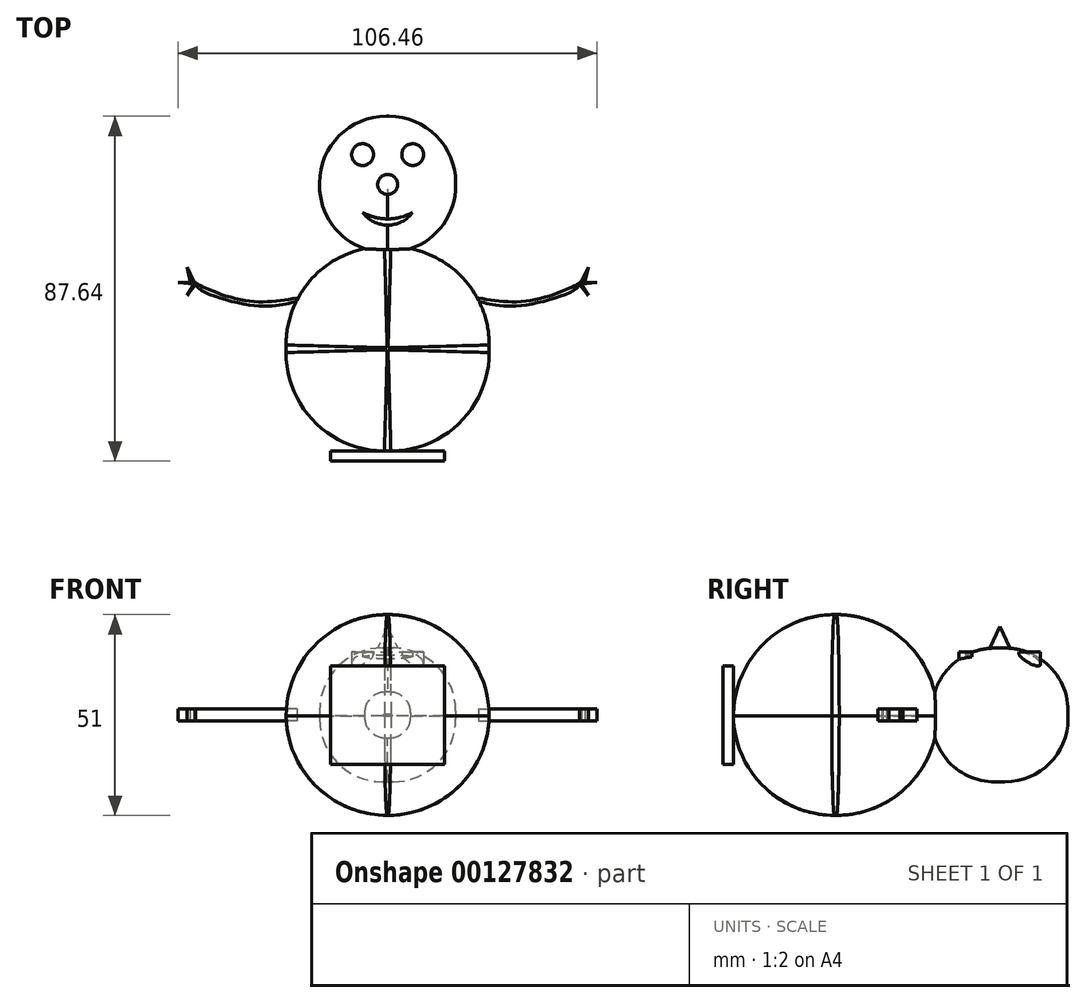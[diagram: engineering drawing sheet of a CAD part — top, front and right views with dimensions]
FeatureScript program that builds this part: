
annotation { "Feature Type Name" : "Feature", "Feature Type Description" : "" }
export const myFeature = defineFeature(function(context is Context, id is Id, definition is map)
    precondition{}
    {
        {
            var Q0;
            Q0=qCreatedBy(makeId("Top.planeOp"),FACE);
            var sketch = newSketch(context, id + "F0", { "sketchPlane" : qUnion([Q0])});
            skLineSegment(sketch, "E0.bottom", {"start": v(0.81, -25.96) * mm, "end": v(-0.81, -25.96) * mm});
            skLineSegment(sketch, "E0.top", {"start": v(0.81, 25.96) * mm, "end": v(-0.81, 25.96) * mm});
            skLineSegment(sketch, "E0.left", {"start": v(25.81, -0.96) * mm, "end": v(25.81, 0.96) * mm});
            skLineSegment(sketch, "E0.right", {"start": v(-25.81, -0.96) * mm, "end": v(-25.81, 0.96) * mm});
            skPoint(sketch, "E0.middle", {"position": v(0, 0) * mm});
            skPoint(sketch, "E1.visualSharp", {"position": v(-25.81, 25.96) * mm});
            skArc(sketch, "E1.filletArc", {"start": v(-0.81, 25.96) * mm, "mid": v(-18.49, 18.63) * mm, "end": v(-25.81, 0.96) * mm});
            skPoint(sketch, "E2.visualSharp", {"position": v(25.81, 25.96) * mm});
            skArc(sketch, "E2.filletArc", {"start": v(25.81, 0.96) * mm, "mid": v(18.49, 18.63) * mm, "end": v(0.81, 25.96) * mm});
            skPoint(sketch, "E3.visualSharp", {"position": v(25.81, -25.96) * mm});
            skArc(sketch, "E3.filletArc", {"start": v(0.81, -25.96) * mm, "mid": v(18.49, -18.63) * mm, "end": v(25.81, -0.96) * mm});
            skPoint(sketch, "E4.visualSharp", {"position": v(-25.81, -25.96) * mm});
            skArc(sketch, "E4.filletArc", {"start": v(-25.81, -0.96) * mm, "mid": v(-18.49, -18.63) * mm, "end": v(-0.81, -25.96) * mm});
            skSolve(sketch);
        }
        {
            var Q0;
            Q0 = qSketchRegion(id + "F0", true);
            extrude(context, id + "F1", {"entities" : qUnion([Q0]), "endBound" : BoundingType.SYMMETRIC, "depth" : 51 * mm});
        }
        {
            var Q0;
            Q0=makeQuery(id+"F1.opExtrude","SWEPT_EDGE",EDGE,{"disambiguationData":[OSD([sQuery(id+"F0.wireOp",EDGE,"E0.bottom"),sQuery(id+"F0.wireOp",EDGE,"E3.filletArc")])]});
            var Q1;
            Q1=makeQuery(id+"F1.opExtrude","CAP_EDGE",EDGE,{"disambiguationData":[OSD([sQuery(id+"F0.wireOp",EDGE,"E3.filletArc")])],"isStart":false});
            fillet(context, id + "F2", {"entities" : qUnion([Q0, Q1]), "radius" : 25.7 * mm, "tangentPropagation" : true, "allowEdgeOverflow" : false});
        }
        {
            var Q0;
            Q0=makeQuery(id+"F1.opExtrude","CAP_EDGE",EDGE,{"disambiguationData":[OSD([sQuery(id+"F0.wireOp",EDGE,"E3.filletArc")])],"isStart":true});
            var Q1;
            Q1=makeQuery(id+"F1.opExtrude","SWEPT_EDGE",EDGE,{"disambiguationData":[OSD([sQuery(id+"F0.wireOp",EDGE,"E0.bottom"),sQuery(id+"F0.wireOp",EDGE,"E3.filletArc")])]});
            fillet(context, id + "F3", {"entities" : qUnion([Q0, Q1]), "radius" : 25.7 * mm, "tangentPropagation" : true, "allowEdgeOverflow" : false});
        }
        {
            var Q0;
            Q0=qCreatedBy(makeId("Top.planeOp"),FACE);
            var sketch = newSketch(context, id + "F4", { "sketchPlane" : qUnion([Q0])});
            skPoint(sketch, "E5", {"position": v(0, 41.8) * mm});
            skLineSegment(sketch, "E6.bottom", {"start": v(0.3, 24.5) * mm, "end": v(-0.3, 24.5) * mm});
            skLineSegment(sketch, "E6.top", {"start": v(0.3, 59.1) * mm, "end": v(-0.3, 59.1) * mm});
            skLineSegment(sketch, "E6.left", {"start": v(17.3, 41.5) * mm, "end": v(17.3, 42.1) * mm});
            skLineSegment(sketch, "E6.right", {"start": v(-17.3, 41.5) * mm, "end": v(-17.3, 42.1) * mm});
            skPoint(sketch, "E7.visualSharp", {"position": v(-17.3, 59.1) * mm});
            skArc(sketch, "E7.filletArc", {"start": v(-0.3, 59.1) * mm, "mid": v(-12.33, 54.12) * mm, "end": v(-17.3, 42.1) * mm});
            skPoint(sketch, "E8.visualSharp", {"position": v(17.3, 59.1) * mm});
            skArc(sketch, "E8.filletArc", {"start": v(17.3, 42.1) * mm, "mid": v(12.33, 54.12) * mm, "end": v(0.3, 59.1) * mm});
            skPoint(sketch, "E9.visualSharp", {"position": v(17.3, 24.5) * mm});
            skArc(sketch, "E9.filletArc", {"start": v(0.3, 24.5) * mm, "mid": v(12.33, 29.47) * mm, "end": v(17.3, 41.5) * mm});
            skPoint(sketch, "E10.visualSharp", {"position": v(-17.3, 24.5) * mm});
            skArc(sketch, "E10.filletArc", {"start": v(-17.3, 41.5) * mm, "mid": v(-12.33, 29.47) * mm, "end": v(-0.3, 24.5) * mm});
            skSolve(sketch);
        }
        {
            var Q0;
            Q0 = qSketchRegion(id + "F4", true);
            extrude(context, id + "F5", {"entities" : qUnion([Q0]), "operationType" : NewBodyOperationType.ADD, "endBound" : BoundingType.SYMMETRIC, "depth" : 34 * mm});
        }
        {
            var Q0;
            Q0=makeQuery(id+"F5.opExtrude","SWEPT_EDGE",EDGE,{"disambiguationData":[OSD([sQuery(id+"F4.wireOp",EDGE,"E6.top"),sQuery(id+"F4.wireOp",EDGE,"E8.filletArc")])]});
            var Q1;
            Q1=makeQuery(id+"F5.opExtrude","CAP_EDGE",EDGE,{"disambiguationData":[OSD([sQuery(id+"F4.wireOp",EDGE,"E8.filletArc")])],"isStart":false});
            fillet(context, id + "F6", {"entities" : qUnion([Q0, Q1]), "radius" : 16 * mm, "tangentPropagation" : true, "allowEdgeOverflow" : false});
        }
        {
            var Q0;
            Q0=makeQuery(id+"F5.opExtrude","SWEPT_EDGE",EDGE,{"disambiguationData":[OSD([sQuery(id+"F4.wireOp",EDGE,"E6.top"),sQuery(id+"F4.wireOp",EDGE,"E8.filletArc")])]});
            var Q1;
            Q1=makeQuery(id+"F5.opExtrude","CAP_EDGE",EDGE,{"disambiguationData":[OSD([sQuery(id+"F4.wireOp",EDGE,"E8.filletArc")])],"isStart":true});
            var Q2;
            Q2=makeQuery(id+"F5.opExtrude","SWEPT_EDGE",EDGE,{"disambiguationData":[OSD([sQuery(id+"F4.wireOp",EDGE,"E6.top"),sQuery(id+"F4.wireOp",EDGE,"E8.filletArc")])]});
            var Q3;
            Q3=makeQuery(id+"F5.opExtrude","CAP_EDGE",EDGE,{"disambiguationData":[OSD([sQuery(id+"F4.wireOp",EDGE,"E8.filletArc")])],"isStart":true});
            var Q4;
            Q4=makeQuery(id+"F5.opExtrude","SWEPT_EDGE",EDGE,{"disambiguationData":[OSD([sQuery(id+"F4.wireOp",EDGE,"E6.top"),sQuery(id+"F4.wireOp",EDGE,"E8.filletArc")])]});
            var Q5;
            Q5=makeQuery(id+"F5.opExtrude","CAP_EDGE",EDGE,{"disambiguationData":[OSD([sQuery(id+"F4.wireOp",EDGE,"E8.filletArc")])],"isStart":true});
            fillet(context, id + "F7", {"entities" : qUnion([Q0, Q1, Q2, Q3, Q4, Q5]), "radius" : 16 * mm, "tangentPropagation" : true, "allowEdgeOverflow" : false});
        }
        {
            var Q0;
            Q0=makeQuery(id+"F5.opExtrude","CAP_FACE",FACE,{"disambiguationData":[OSD([sQuery(id+"F4.wireOp",EDGE,"E6.bottom"),sQuery(id+"F4.wireOp",EDGE,"E6.top"),sQuery(id+"F4.wireOp",EDGE,"E6.left"),sQuery(id+"F4.wireOp",EDGE,"E6.right"),sQuery(id+"F4.wireOp",EDGE,"E7.filletArc"),sQuery(id+"F4.wireOp",EDGE,"E8.filletArc"),sQuery(id+"F4.wireOp",EDGE,"E9.filletArc"),sQuery(id+"F4.wireOp",EDGE,"E10.filletArc")])],"isStart":false});
            var sketch = newSketch(context, id + "F8", { "sketchPlane" : qUnion([Q0])});
            skCircle(sketch, "E11", {"center": v(0, 41.75) * mm, "radius": 2.55 * mm});
            skSolve(sketch);
        }
        {
            var Q0;
            Q0 = qSketchRegion(id + "F8", true);
            extrude(context, id + "F9", {"entities" : qUnion([Q0]), "depth" : 6 * mm, "hasDraft" : true, "draftAngle" : 25 * degree, "draftPullDirection" : true});
        }
        {
            var Q0;
            Q0=qCreatedBy(makeId("Top.planeOp"),FACE);
            var sketch = newSketch(context, id + "F10", { "sketchPlane" : qUnion([Q0])});
            skPoint(sketch, "E12.middle", {"position": v(0, 42) * mm});
            skCircle(sketch, "E13", {"center": v(-6.36, 49.34) * mm, "radius": 2.78 * mm});
            skCircle(sketch, "E14", {"center": v(6.36, 49.34) * mm, "radius": 2.77 * mm});
            skArc(sketch, "E15", {"start": v(-6.36, 34.67) * mm, "mid": v(0, 31.4) * mm, "end": v(6.36, 34.67) * mm});
            skArc(sketch, "E16", {"start": v(-6.36, 34.67) * mm, "mid": v(0, 33) * mm, "end": v(6.36, 34.67) * mm});
            skSolve(sketch);
        }
        {
            var Q0;
            Q0 = qSketchRegion(id + "F10", true);
            extrude(context, id + "F11", {"entities" : qUnion([Q0]), "operationType" : NewBodyOperationType.ADD, "depth" : 16 * mm});
        }
        {
            var Q0;
            Q0=qCreatedBy(makeId("Top.planeOp"),FACE);
            var sketch = newSketch(context, id + "F12", { "sketchPlane" : qUnion([Q0])});
            skFitSpline(sketch, "E17", {"points": [v(-23.02, 12.93) * mm, v(-35.77, 12.2) * mm, v(-47.6, 16.07) * mm, v(-49.26, 17.18) * mm], "startDerivative": vector(-29.06, -5.1) * mm, "endDerivative": vector(-7.18, 5.82) * mm});
            skLineSegment(sketch, "E18", {"start": v(-49.26, 17.18) * mm, "end": v(-51.01, 20.73) * mm});
            skLineSegment(sketch, "E19", {"start": v(-48.86, 16.86) * mm, "end": v(-53.23, 16.86) * mm});
            skLineSegment(sketch, "E20", {"start": v(-48.86, 16.86) * mm, "end": v(-51.01, 13.53) * mm});
            skFitSpline(sketch, "E21.MirrorCS", {"points": [v(23.02, 12.93) * mm, v(35.77, 12.2) * mm, v(47.6, 16.07) * mm, v(49.26, 17.18) * mm], "startDerivative": vector(29.06, -5.1) * mm, "endDerivative": vector(7.18, 5.82) * mm});
            skLineSegment(sketch, "E22.MirrorCS", {"start": v(49.26, 17.18) * mm, "end": v(51.01, 20.73) * mm});
            skLineSegment(sketch, "E23.MirrorCS", {"start": v(48.86, 16.86) * mm, "end": v(53.23, 16.86) * mm});
            skLineSegment(sketch, "E24.MirrorCS", {"start": v(48.86, 16.86) * mm, "end": v(51.01, 13.53) * mm});
            skFitSpline(sketch, "E25", {"points": [v(-23.03, 12.07) * mm, v(-27.08, 11.14) * mm, v(-35.79, 11.24) * mm, v(-47.92, 15.28) * mm, v(-48.86, 16.86) * mm], "startDerivative": vector(-18.36, -5.03) * mm, "endDerivative": vector(-2.73, 11.14) * mm});
            skLineSegment(sketch, "E26", {"start": v(-51.01, 13.53) * mm, "end": v(-48.74, 16.35) * mm});
            skLineSegment(sketch, "E27", {"start": v(-51.01, 20.73) * mm, "end": v(-50.14, 17.18) * mm});
            skPoint(sketch, "E27.endSnap0", {"position": v(-50.14, 18.96) * mm});
            skLineSegment(sketch, "E28", {"start": v(-53.23, 16.86) * mm, "end": v(-48.74, 16.35) * mm});
            skFitSpline(sketch, "E29.MirrorCS", {"points": [v(23.03, 12.07) * mm, v(27.08, 11.14) * mm, v(35.79, 11.24) * mm, v(47.92, 15.28) * mm, v(48.86, 16.86) * mm], "startDerivative": vector(18.36, -5.03) * mm, "endDerivative": vector(2.73, 11.14) * mm});
            skLineSegment(sketch, "E30.MirrorCS", {"start": v(51.01, 13.53) * mm, "end": v(48.74, 16.35) * mm});
            skLineSegment(sketch, "E31.MirrorCS", {"start": v(53.23, 16.86) * mm, "end": v(48.74, 16.35) * mm});
            skLineSegment(sketch, "E32.MirrorCS", {"start": v(51.01, 20.73) * mm, "end": v(50.14, 17.18) * mm});
            skLineSegment(sketch, "E33", {"start": v(-23.03, 12.07) * mm, "end": v(-23.02, 12.93) * mm});
            skLineSegment(sketch, "E34", {"start": v(23.03, 12.07) * mm, "end": v(23.02, 12.93) * mm});
            skLineSegment(sketch, "E35", {"start": v(-47.92, 15.28) * mm, "end": v(-47.6, 16.07) * mm});
            skLineSegment(sketch, "E36", {"start": v(-50.14, 17.18) * mm, "end": v(-48.86, 16.86) * mm});
            skLineSegment(sketch, "E37", {"start": v(47.92, 15.28) * mm, "end": v(47.6, 16.07) * mm});
            skLineSegment(sketch, "E38", {"start": v(50.14, 17.18) * mm, "end": v(48.86, 16.86) * mm});
            skSolve(sketch);
        }
        {
            var Q0;
            Q0 = qSketchRegion(id + "F12", true);
            extrude(context, id + "F13", {"entities" : qUnion([Q0]), "endBound" : BoundingType.SYMMETRIC, "depth" : 3 * mm});
        }
        {
            var Q0;
            Q0=qCreatedBy(makeId("Top.planeOp"),FACE);
            var sketch = newSketch(context, id + "F14", { "sketchPlane" : qUnion([Q0])});
            skLineSegment(sketch, "E39.bottom", {"start": v(14.5, -28.54) * mm, "end": v(-14.5, -28.54) * mm});
            skLineSegment(sketch, "E39.top", {"start": v(14.5, -25.95) * mm, "end": v(-14.5, -25.95) * mm});
            skLineSegment(sketch, "E39.left", {"start": v(14.5, -28.54) * mm, "end": v(14.5, -25.95) * mm});
            skLineSegment(sketch, "E39.right", {"start": v(-14.5, -28.54) * mm, "end": v(-14.5, -25.95) * mm});
            skPoint(sketch, "E39.middle", {"position": v(0, -27.25) * mm});
            skSolve(sketch);
        }
        {
            var Q0;
            Q0 = qSketchRegion(id + "F14", true);
            extrude(context, id + "F15", {"entities" : qUnion([Q0]), "operationType" : NewBodyOperationType.ADD, "endBound" : BoundingType.SYMMETRIC, "depth" : 25 * mm});
        }
    });
